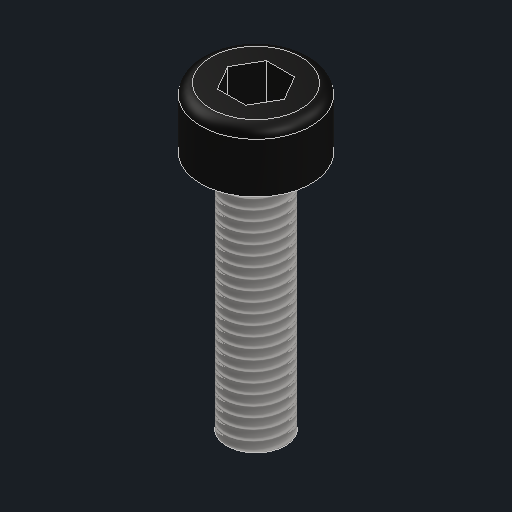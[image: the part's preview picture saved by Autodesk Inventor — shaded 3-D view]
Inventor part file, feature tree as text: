
AUTODESK INVENTOR PART (.ipt)
format: ipt  version: 2025.1 (Build 291241000, 241)  size: 269,824 bytes
history: native  units: mm
features: extrude x3, sketch x1, fillet x1, thread x1
ambient origin geometry x8: Origin, YZ Plane, XZ Plane, XY Plane, X Axis, Y Axis, Z Axis, Center Point
bodies: Solid1 (feature_tree)
feature tree (6):
  sketch  "Sketch1"  dims[d0=2.93mm d1=5.5mm d2=3.0mm d3=0.0mm d4=12.0mm d5=0.0mm d8=2.45mm d9=2.0mm d10=0.0mm d11=0.5mm d12=16.0mm d13=0.0mm]
  extrude  "Extrusion1"  Depth=0.5mm
  extrude  "Extrusion2"  Depth=3.0mm TaperAngle=0.0deg
  extrude  "Extrusion3"  Depth=12.0mm
  fillet  "Fillet1"  [1 undecoded]
  thread  "Thread2"  [1 undecoded]
note: 2 required parameter values undecoded (feature->parameter linkage not recoverable at this tier; creation-order binding heuristic only, values carry confidence <= 0.55)
